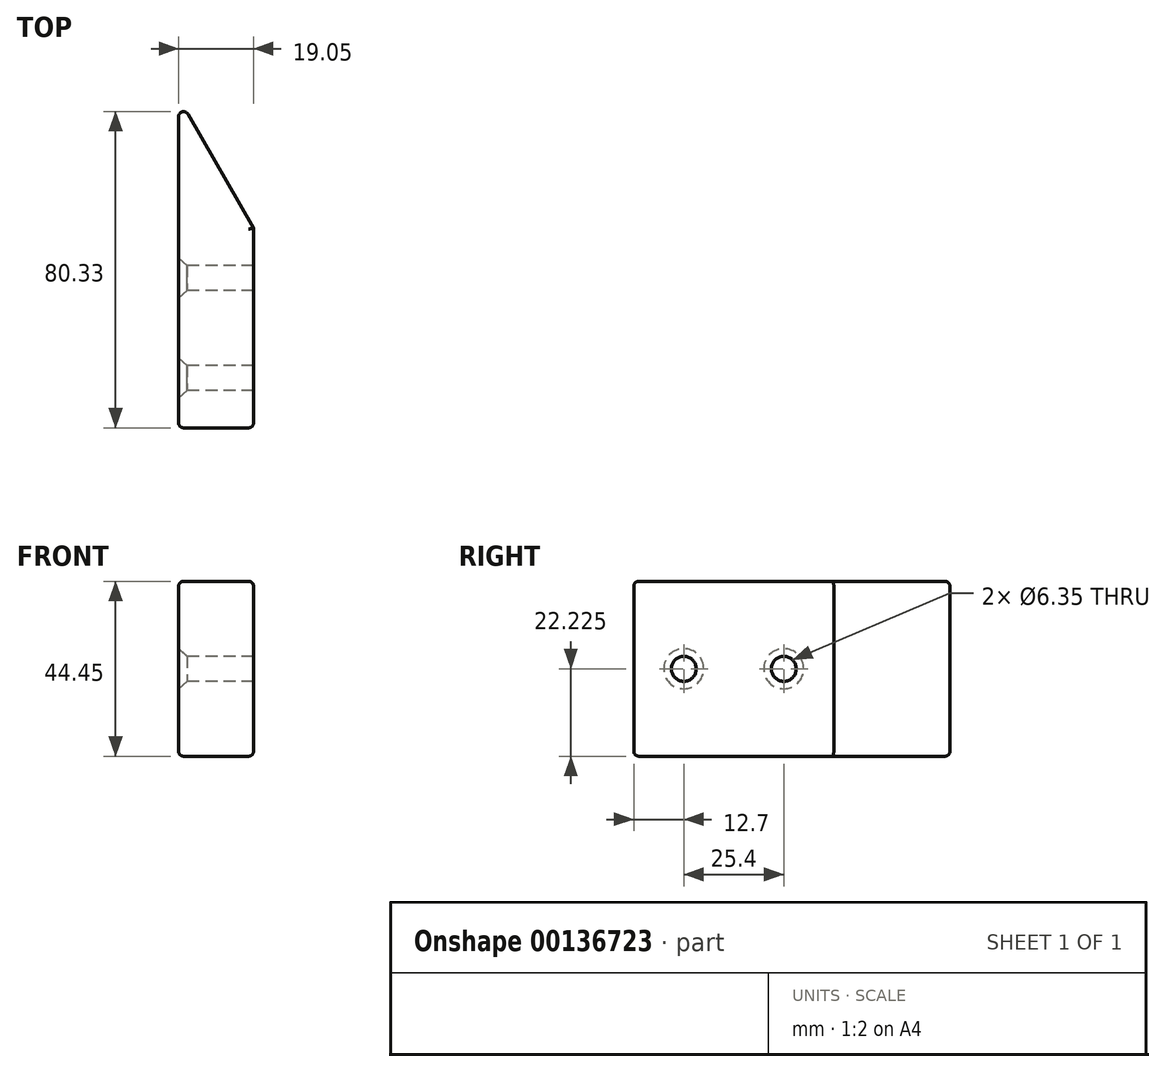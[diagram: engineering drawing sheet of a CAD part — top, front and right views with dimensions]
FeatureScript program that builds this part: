
annotation { "Feature Type Name" : "Feature", "Feature Type Description" : "" }
export const myFeature = defineFeature(function(context is Context, id is Id, definition is map)
    precondition{}
    {
        {
            var Q0;
            Q0=qCreatedBy(makeId("Top.planeOp"),FACE);
            var sketch = newSketch(context, id + "F0", { "sketchPlane" : qUnion([Q0])});
            skLineSegment(sketch, "E0", {"start": v(0, 0) * mm, "end": v(19.05, 0) * mm});
            skLineSegment(sketch, "E1", {"start": v(19.05, 0) * mm, "end": v(19.05, 50.8) * mm});
            skLineSegment(sketch, "E2", {"start": v(19.05, 50.8) * mm, "end": v(0, 83.8) * mm});
            skLineSegment(sketch, "E3", {"start": v(0, 83.8) * mm, "end": v(0, 0) * mm});
            skSolve(sketch);
        }
        {
            var Q0;
            Q0=makeQuery(id+"F0.imprint","IMPRINT",FACE,{"disambiguationData":[TD([[makeQuery(id+"F0.imprint","IMPRINT",EDGE,{"derivedFrom":sQuery(id+"F0.wireOp",EDGE,"E0")}),1.0]])]});
            extrude(context, id + "F1", {"entities" : qUnion([Q0]), "depth" : 44.45 * mm});
        }
        {
            var Q0;
            Q0=makeQuery(id+"F1.opExtrude","SWEPT_FACE",FACE,{"disambiguationData":[OSD([sQuery(id+"F0.wireOp",EDGE,"E3")])]});
            var sketch = newSketch(context, id + "F2", { "sketchPlane" : qUnion([Q0])});
            skPoint(sketch, "E4", {"position": v(-12.7, 22.23) * mm});
            skPoint(sketch, "E5", {"position": v(-38.1, 22.23) * mm});
            skLineSegment(sketch, "E6", {"start": v(-101.98, 22.23) * mm, "end": v(14.04, 22.23) * mm, "construction": true});
            skSolve(sketch);
        }
        {
            var Q0;
            Q0=sQuery(id+"F2.wireOp",VERTEX,"E4");
            var Q1;
            Q1=sQuery(id+"F2.wireOp",VERTEX,"E5");
            var Q2;
            Q2=sQuery(id+"F2.wireOp",VERTEX,"fd414b69-aa0b-4d1e-85eb-326c3dd4f586");
            var Q3;
            Q3=makeQuery(id+"F1.opExtrude","SWEPT_BODY",BODY,{"disambiguationData":[OSD([sQuery(id+"F0.wireOp",EDGE,"E0"),sQuery(id+"F0.wireOp",EDGE,"E1"),sQuery(id+"F0.wireOp",EDGE,"E2"),sQuery(id+"F0.wireOp",EDGE,"E3")])]});
            hole(context, id + "F3", {"style" : HoleStyle.C_SINK, "endStyle" : HoleEndStyle.THROUGH, "holeDiameter" : 6.35 * mm, "cSinkDiameter" : 10.16 * mm, "cSinkAngle" : 82 * degree, "startFromSketch" : true, "locations" : qUnion([Q0, Q1, Q2]), "scope" : qUnion([Q3]), "isTappedThrough" : true});
        }
        {
            var Q0;
            Q0=makeQuery(id+"F1.opExtrude","SWEPT_EDGE",EDGE,{"disambiguationData":[OSD([sQuery(id+"F0.wireOp",EDGE,"E2"),sQuery(id+"F0.wireOp",EDGE,"E3")])]});
            fillet(context, id + "F4", {"entities" : qUnion([Q0]), "radius" : 1.27 * mm, "tangentPropagation" : true, "allowEdgeOverflow" : false});
        }
        {
            var Q0;
            Q0=makeQuery(id+"F1.opExtrude","CAP_FACE",FACE,{"disambiguationData":[OSD([sQuery(id+"F0.wireOp",EDGE,"E0"),sQuery(id+"F0.wireOp",EDGE,"E1"),sQuery(id+"F0.wireOp",EDGE,"E2"),sQuery(id+"F0.wireOp",EDGE,"E3")])],"isStart":false});
            var Q1;
            Q1=makeQuery(id+"F1.opExtrude","CAP_FACE",FACE,{"disambiguationData":[OSD([sQuery(id+"F0.wireOp",EDGE,"E0"),sQuery(id+"F0.wireOp",EDGE,"E1"),sQuery(id+"F0.wireOp",EDGE,"E2"),sQuery(id+"F0.wireOp",EDGE,"E3")])],"isStart":true});
            var Q2;
            Q2=makeQuery(id+"F1.opExtrude","SWEPT_EDGE",EDGE,{"disambiguationData":[OSD([sQuery(id+"F0.wireOp",EDGE,"E0"),sQuery(id+"F0.wireOp",EDGE,"E3")])]});
            var Q3;
            Q3=makeQuery(id+"F1.opExtrude","SWEPT_EDGE",EDGE,{"disambiguationData":[OSD([sQuery(id+"F0.wireOp",EDGE,"E0"),sQuery(id+"F0.wireOp",EDGE,"E1")])]});
            var Q4;
            Q4=makeQuery(id+"F3.hole-2.boolean.opBoolean","COPY",EDGE,{"derivedFrom":makeQuery(id+"F3.hole-2.opRevolve","SWEPT_EDGE",EDGE,{"disambiguationData":[OSD([sQuery(id+"F3.hole-2.sketch.wireOp",EDGE,"core_line_2"),sQuery(id+"F3.hole-2.sketch.wireOp",EDGE,"core_line_3")])]})});
            var Q5;
            Q5=makeQuery(id+"F3.hole-2.boolean.opBoolean","INTERSECT",EDGE,{"derivedFrom":[makeQuery(id+"F1.opExtrude","SWEPT_FACE",FACE,{"disambiguationData":[OSD([sQuery(id+"F0.wireOp",EDGE,"E2")])]}),makeQuery(id+"F3.hole-2.opRevolve","SWEPT_FACE",FACE,{"disambiguationData":[OSD([sQuery(id+"F3.hole-2.sketch.wireOp",EDGE,"core_line_2")])]})]});
            fillet(context, id + "F5", {"entities" : qUnion([Q0, Q1, Q2, Q3, Q4, Q5]), "radius" : 1.27 * mm, "tangentPropagation" : true, "allowEdgeOverflow" : false});
        }
    });
